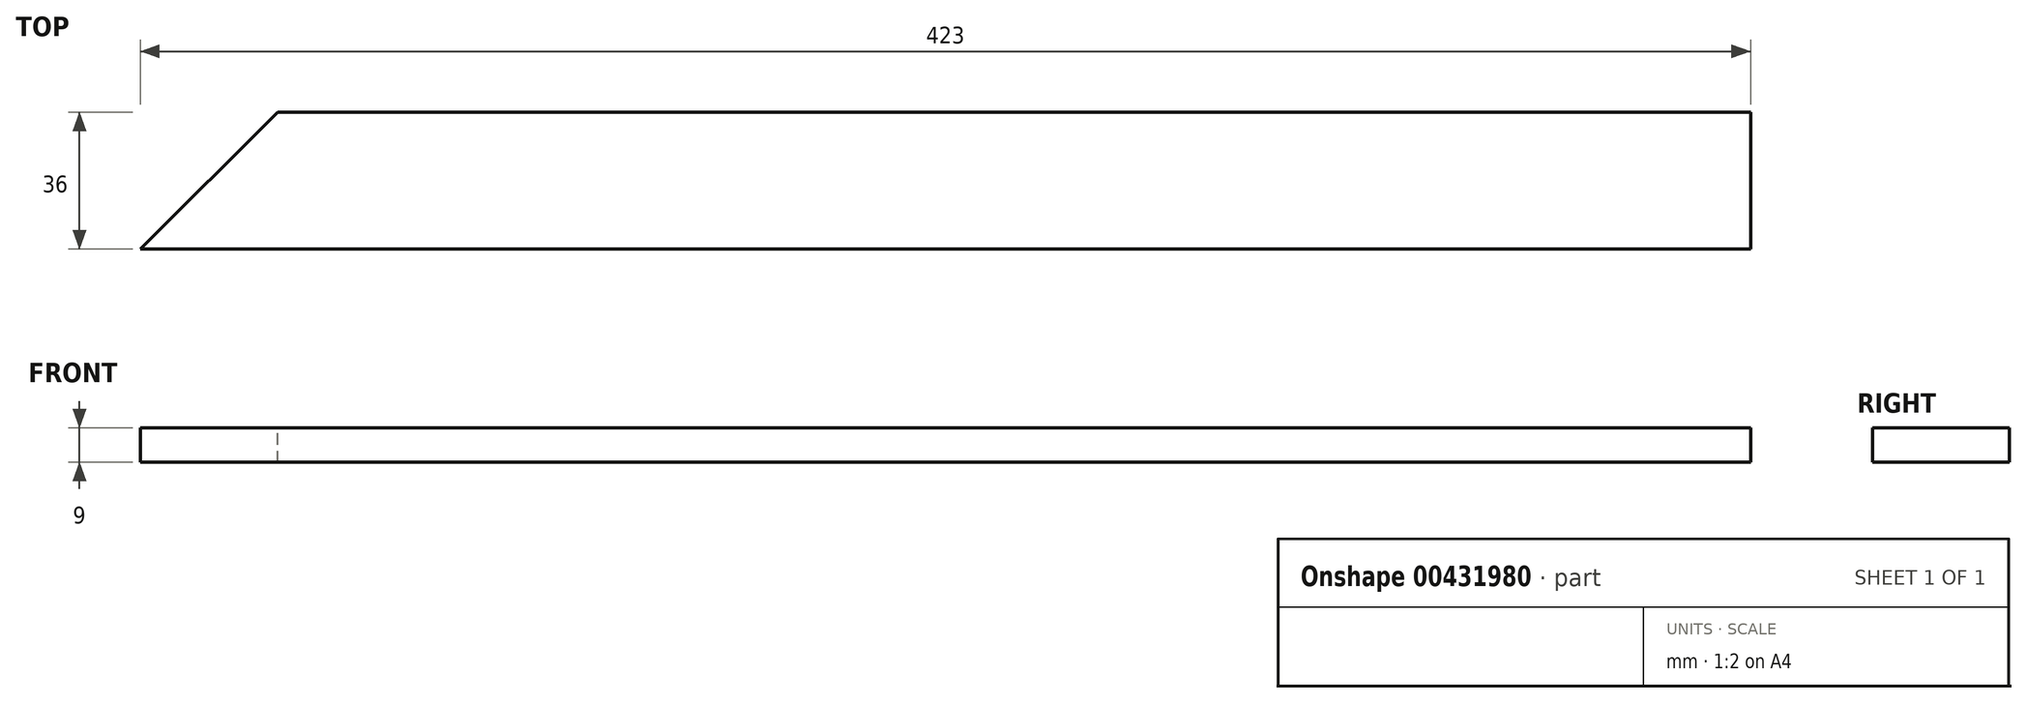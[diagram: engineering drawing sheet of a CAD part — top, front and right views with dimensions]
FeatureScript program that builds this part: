
annotation { "Feature Type Name" : "Feature", "Feature Type Description" : "" }
export const myFeature = defineFeature(function(context is Context, id is Id, definition is map)
    precondition{}
    {
        {
            var Q0;
            Q0=qCreatedBy(makeId("Top.planeOp"),FACE);
            var sketch = newSketch(context, id + "F0", { "sketchPlane" : qUnion([Q0])});
            skLineSegment(sketch, "E0.bottom", {"start": v(-211.5, 18) * mm, "end": v(211.5, 18) * mm});
            skLineSegment(sketch, "E0.top", {"start": v(-211.5, -18) * mm, "end": v(211.5, -18) * mm});
            skLineSegment(sketch, "E0.left", {"start": v(-211.5, 18) * mm, "end": v(-211.5, -18) * mm});
            skLineSegment(sketch, "E0.right", {"start": v(211.5, 18) * mm, "end": v(211.5, -18) * mm});
            skPoint(sketch, "E0.middle", {"position": v(0, 0) * mm});
            skSolve(sketch);
        }
        {
            var Q0;
            Q0=qSketchRegion(id+"F0",true);
            extrude(context, id + "F1", {"entities" : qUnion([Q0]), "depth" : 9 * mm, "offsetDistance" : 25 * mm});
        }
        {
            var Q0;
            Q0=makeQuery(id+"F1.opExtrude","SWEPT_EDGE",EDGE,{"disambiguationData":[OSD([sQuery(id+"F0.wireOp",EDGE,"E0.bottom"),sQuery(id+"F0.wireOp",EDGE,"E0.left")])]});
            chamfer(context, id + "F2", {"entities" : qUnion([Q0]), "width" : 36 * mm, "tangentPropagation" : true});
        }
    });
